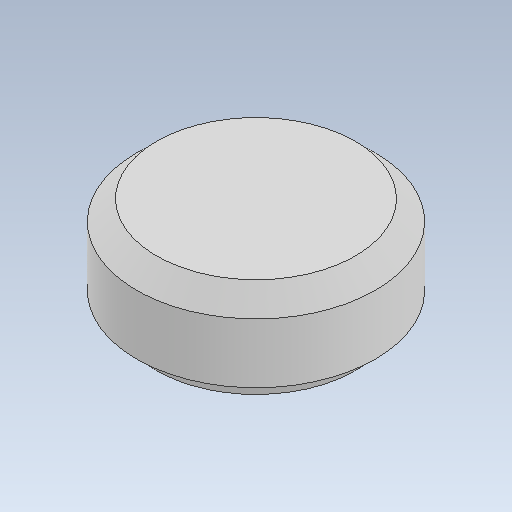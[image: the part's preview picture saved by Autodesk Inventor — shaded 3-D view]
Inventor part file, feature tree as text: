
AUTODESK INVENTOR PART (.ipt)
format: ipt  version: 2020 (Build 240168000, 168)  size: 100,864 bytes
history: native  units: mm
features: extrude x1, chamfer x1, sketch x1
ambient origin geometry x8: Origin, YZ Plane, XZ Plane, XY Plane, X Axis, Y Axis, Z Axis, Center Point
bodies: Solid1 (feature_tree)
feature tree (3):
  extrude  "Extrusion1"  Depth=2.5mm TaperAngle=0.0deg
  chamfer  "Chamfer1"  Distance=0.5mm Angle=45.0deg
  sketch  "Sketch1"  dims[d0=6.0mm d1=2.5mm d2=0.0mm d3=0.5mm d4=2.0mm d5=45.0deg]
